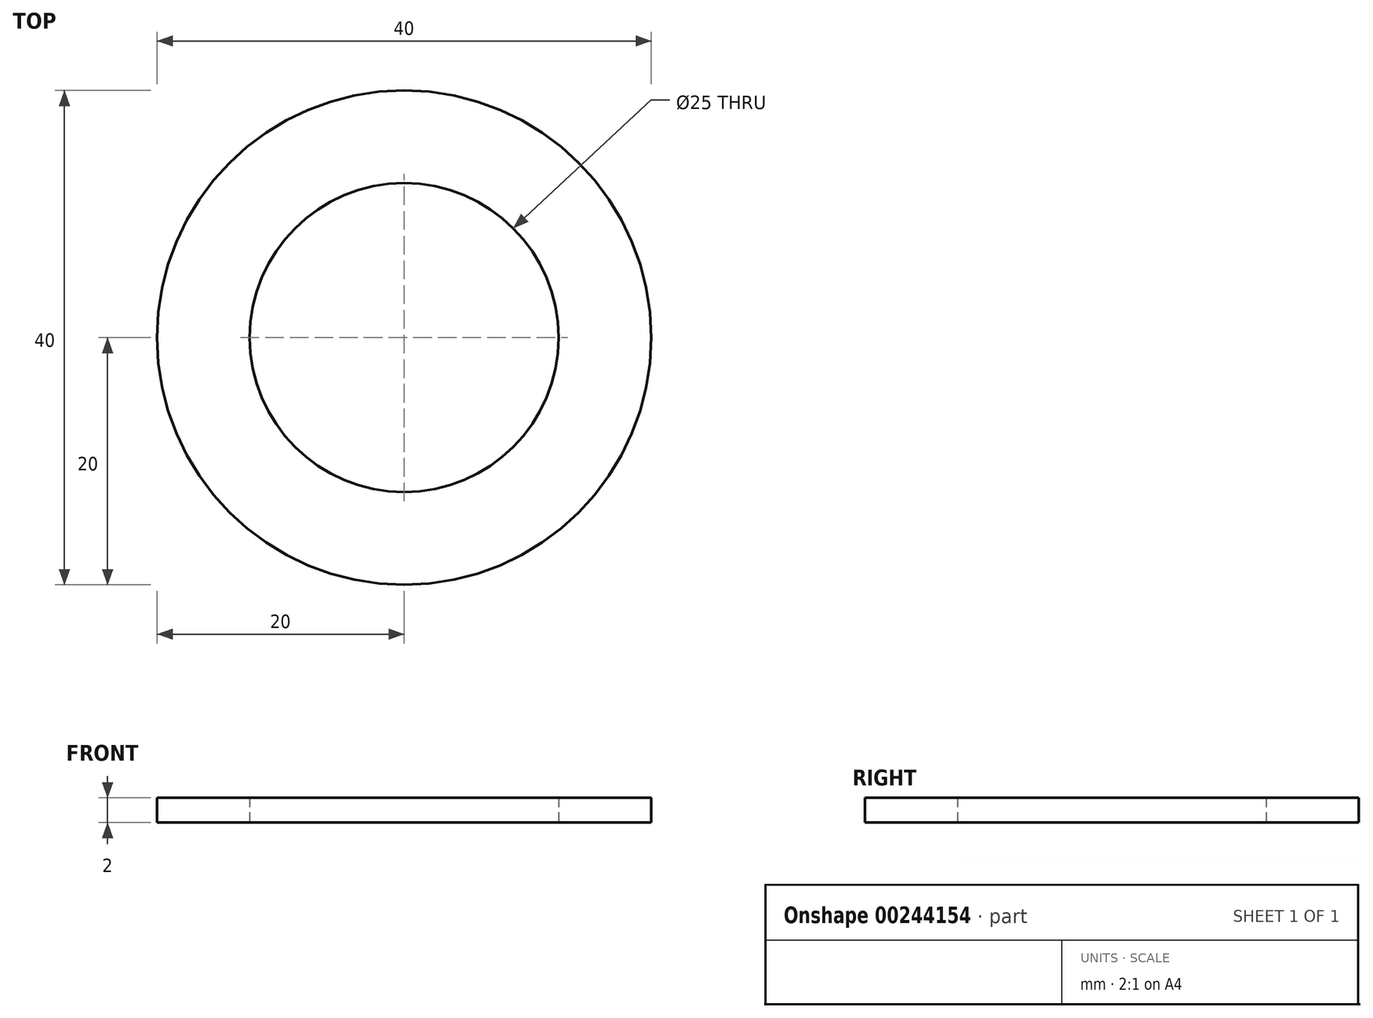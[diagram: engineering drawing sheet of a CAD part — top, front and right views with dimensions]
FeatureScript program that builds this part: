
annotation { "Feature Type Name" : "Feature", "Feature Type Description" : "" }
export const myFeature = defineFeature(function(context is Context, id is Id, definition is map)
    precondition{}
    {
        {
            var Q0;
            Q0=qCreatedBy(makeId("Top.planeOp"),FACE);
            var sketch = newSketch(context, id + "F0", { "sketchPlane" : qUnion([Q0])});
            skCircle(sketch, "E0", {"center": v(0, 0) * mm, "radius": 12.5 * mm});
            skCircle(sketch, "E1", {"center": v(0, 0) * mm, "radius": 20 * mm});
            skSolve(sketch);
        }
        {
            var Q0;
            Q0=makeQuery(id+"F0.imprint","IMPRINT",FACE,{"disambiguationData":[TD([[makeQuery(id+"F0.imprint","IMPRINT",EDGE,{"derivedFrom":sQuery(id+"F0.wireOp",EDGE,"E0")}),-1.0]])]});
            extrude(context, id + "F1", {"entities" : qUnion([Q0]), "depth" : 2 * mm});
        }
    });
